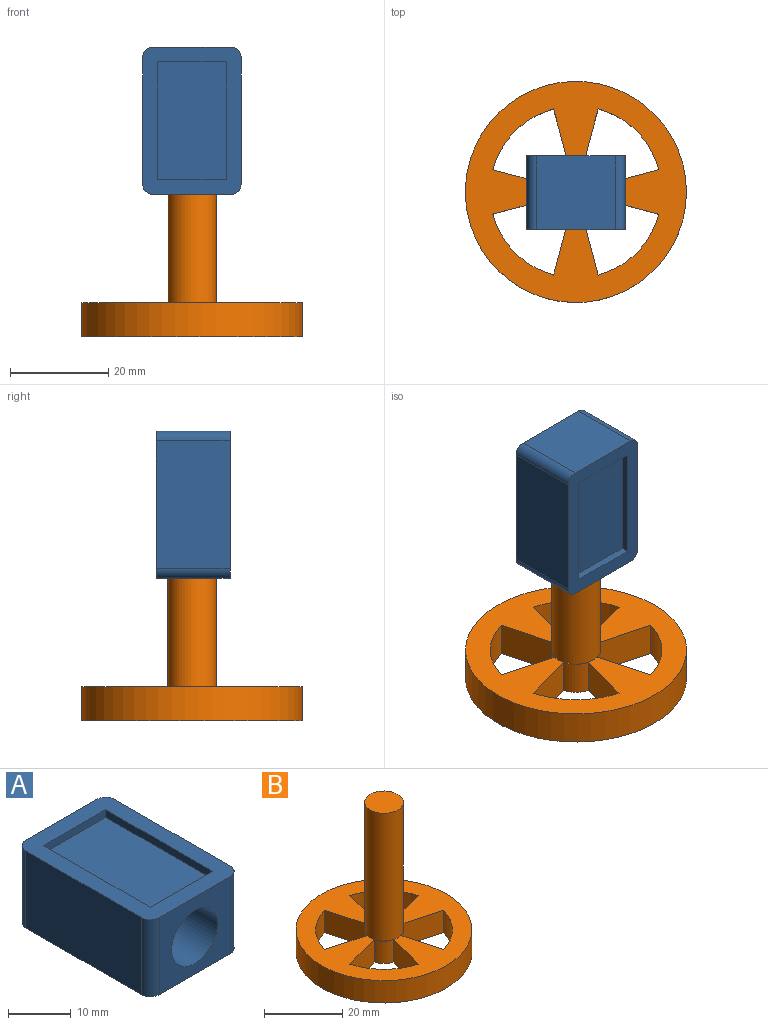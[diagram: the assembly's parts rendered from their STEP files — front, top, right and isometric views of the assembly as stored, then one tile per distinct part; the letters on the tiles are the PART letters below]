
ASSEMBLY  parts=2 mates=1
PART A: 17 faces, bbox 20x30x15 mm
  f0: plane 30x20mm, normal (0,0,1), area 260.6mm2, adj f1,f2,f3,f4,f5,f6,f7,f8
  f1: plane 26x15mm, normal (1,0,0), area 390mm2, adj f0,f2,f8,f9
  f2: cylinder r=2mm len=15mm, axis (0,0,-1), area 47.1mm2, adj f0,f1,f3,f9
  f3: plane 16x15mm, normal (0,1,0), area 240mm2, adj f0,f2,f4,f9
  f4: cylinder r=2mm len=15mm, axis (0,0,-1), area 47.1mm2, adj f0,f3,f5,f9
  f5: plane 26x15mm, normal (-1,0,0), area 390mm2, adj f0,f4,f6,f9
  f6: cylinder r=2mm len=15mm, axis (0,0,-1), area 47.1mm2, adj f0,f5,f7,f9
  f7: plane 16x15mm, normal (0,-1,0), area 155.9mm2, adj f0,f6,f8,f9,f15
  f8: cylinder r=2mm len=15mm, axis (0,0,-1), area 47.1mm2, adj f0,f1,f7,f9
  f9: plane 30x20mm, normal (0,0,-1), area 596.6mm2, adj f1,f2,f3,f4,f5,f6,f7,f8
  f10: plane 14x1.5mm, normal (0,1,0), area 21mm2, adj f0,f11,f13,f14
  f11: plane 24x1.5mm, normal (-1,0,0), area 36mm2, adj f0,f10,f12,f14
  f12: plane 14x1.5mm, normal (0,-1,0), area 21mm2, adj f0,f11,f13,f14
  f13: plane 24x1.5mm, normal (1,0,0), area 36mm2, adj f0,f10,f12,f14
  f14: plane 24x14mm, normal (0,0,1), area 336mm2, adj f10,f11,f12,f13
  f15: cylinder r=5.17mm len=18mm, axis (0,-1,0), area 585.3mm2, adj f7,f16
  f16: plane 10.35x10.35mm, normal (0,-1,0), area 84.1mm2, adj f15
PART B: 21 faces, bbox 45x45x47 mm
  f0: plane 12.07x7mm, normal (0.97,0.26,0), area 87.5mm2, adj f1,f16,f17,f18
  f1: cylinder r=5mm len=7mm, axis (0,0,-1), area 36.7mm2, adj f0,f2,f17,f18
  f2: plane 12.07x7mm, normal (-0.26,-0.97,0), area 87.5mm2, adj f1,f16,f17,f18
  f3: plane 12.07x7mm, normal (-0.26,0.97,0), area 87.5mm2, adj f4,f12,f17,f18
  f4: cylinder r=5mm len=7mm, axis (0,0,-1), area 36.7mm2, adj f3,f5,f17,f18
  f5: plane 12.07x7mm, normal (0.97,-0.26,0), area 87.5mm2, adj f4,f12,f17,f18
  f6: plane 12.07x7mm, normal (-0.97,-0.26,0), area 87.5mm2, adj f7,f13,f17,f18
  f7: cylinder r=5mm len=7mm, axis (0,0,-1), area 36.7mm2, adj f6,f8,f17,f18
  f8: plane 12.07x7mm, normal (0.26,0.97,0), area 87.5mm2, adj f7,f13,f17,f18
  f9: plane 12.07x7mm, normal (-0.97,0.26,0), area 87.5mm2, adj f10,f15,f17,f18
  f10: cylinder r=17.5mm len=12.37mm, axis (0,0,-1), area 128.3mm2, adj f9,f11,f17,f18
  f11: plane 12.07x7mm, normal (0.26,-0.97,0), area 87.5mm2, adj f10,f15,f17,f18
  f12: cylinder r=17.5mm len=12.37mm, axis (0,0,-1), area 128.3mm2, adj f3,f5,f17,f18
  f13: cylinder r=17.5mm len=12.37mm, axis (0,0,-1), area 128.3mm2, adj f6,f8,f17,f18
  f14: cylinder r=22.5mm len=45mm, axis (0,0,-1), area 989.6mm2, adj f17,f18
  f15: cylinder r=5mm len=7mm, axis (0,0,-1), area 36.7mm2, adj f9,f11,f17,f18
  f16: cylinder r=17.5mm len=12.37mm, axis (0,0,-1), area 128.3mm2, adj f0,f2,f17,f18
  f17: plane 45x45mm, normal (0,0,1), area 924.4mm2, adj f0,f1,f2,f3,f4,f5,f6,f7
  f18: plane 45x45mm, normal (0,0,-1), area 1001.4mm2, adj f0,f1,f2,f3,f4,f5,f6,f7
  f19: cylinder r=4.95mm len=40mm, axis (0,0,-1), area 1244.1mm2, adj f17,f20
  f20: plane 9.9x9.9mm, normal (0,0,1), area 77mm2, adj f19
PLACE A rot(axis=(1,0,0),90deg) t=(-39.09,5.62,37.9)mm
PLACE B t=(-39.09,-1.63,-6.1)mm
MATE fastened A.f15 <-> B.f19  axis (0,0,-1) through (-39.09,-1.63,40.9)mm
